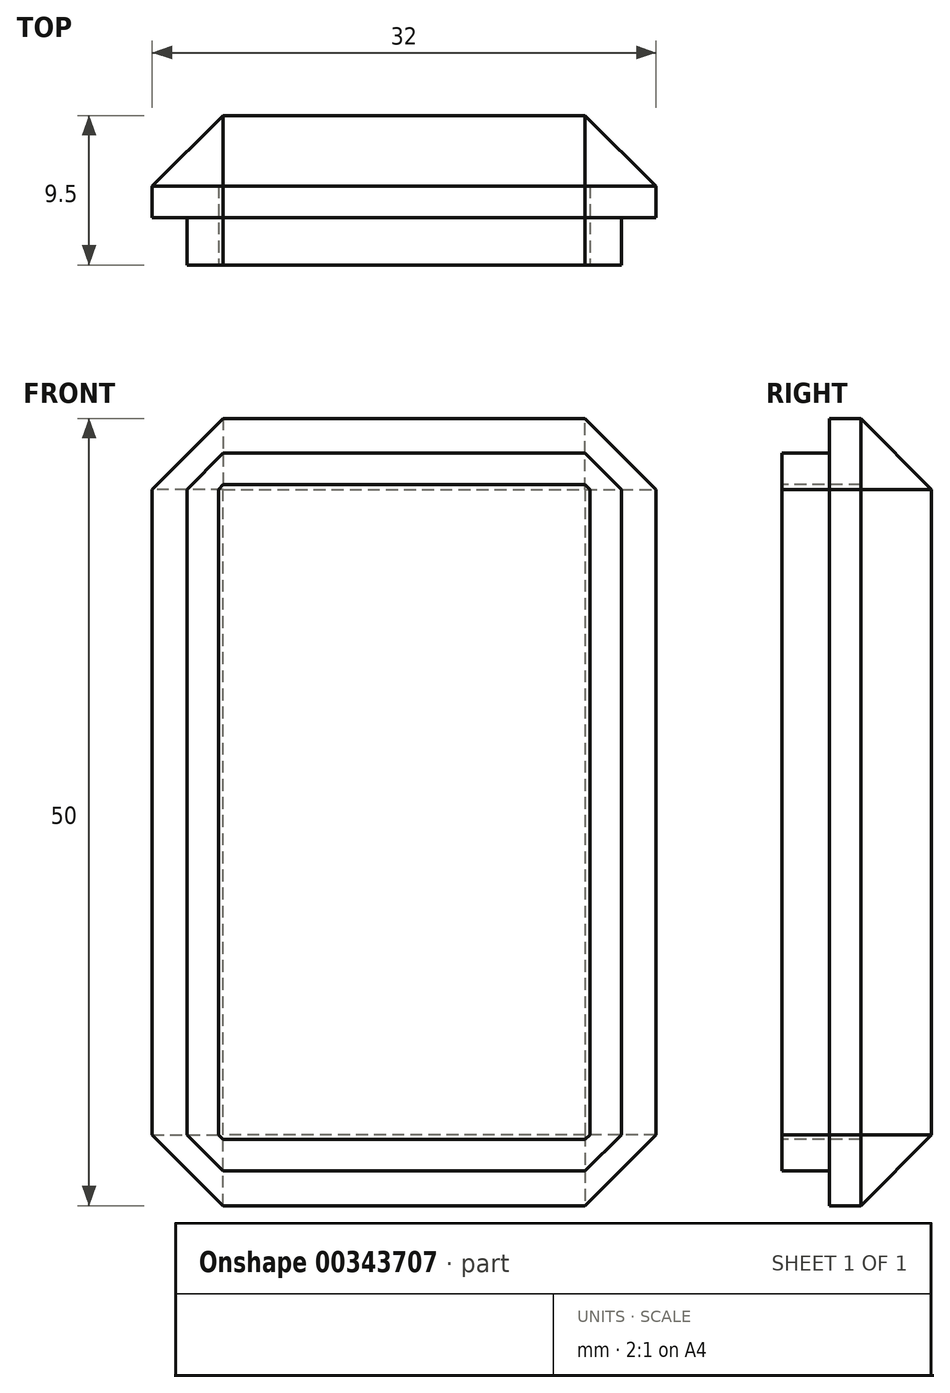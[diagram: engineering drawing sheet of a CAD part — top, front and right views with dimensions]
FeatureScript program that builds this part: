
annotation { "Feature Type Name" : "Feature", "Feature Type Description" : "" }
export const myFeature = defineFeature(function(context is Context, id is Id, definition is map)
    precondition{}
    {
        {
            var Q0;
            Q0=qCreatedBy(makeId("Front.planeOp"),FACE);
            var sketch = newSketch(context, id + "F0", { "sketchPlane" : qUnion([Q0])});
            skLineSegment(sketch, "E0.bottom", {"start": v(0, 0) * mm, "end": v(32, 0) * mm});
            skLineSegment(sketch, "E0.top", {"start": v(0, 50) * mm, "end": v(32, 50) * mm});
            skLineSegment(sketch, "E0.left", {"start": v(0, 0) * mm, "end": v(0, 50) * mm});
            skLineSegment(sketch, "E0.right", {"start": v(32, 0) * mm, "end": v(32, 50) * mm});
            skSolve(sketch);
        }
        {
            var Q0;
            Q0 = qSketchRegion(id + "F0", true);
            extrude(context, id + "F1", {"entities" : qUnion([Q0]), "depth" : 15 * mm, "offsetDistance" : 25.4 * mm});
        }
        {
            var Q0;
            Q0=makeQuery(id+"F1.opExtrude","SWEPT_FACE",FACE,{"disambiguationData":[OSD([sQuery(id+"F0.wireOp",EDGE,"E0.left")])]});
            var Q1;
            Q1=makeQuery(id+"F1.opExtrude","CAP_FACE",FACE,{"disambiguationData":[OSD([sQuery(id+"F0.wireOp",EDGE,"E0.bottom"),sQuery(id+"F0.wireOp",EDGE,"E0.top"),sQuery(id+"F0.wireOp",EDGE,"E0.left"),sQuery(id+"F0.wireOp",EDGE,"E0.right")])],"isStart":true});
            var Q2;
            Q2=makeQuery(id+"F1.opExtrude","SWEPT_FACE",FACE,{"disambiguationData":[OSD([sQuery(id+"F0.wireOp",EDGE,"E0.top")])]});
            var Q3;
            Q3=makeQuery(id+"F1.opExtrude","SWEPT_FACE",FACE,{"disambiguationData":[OSD([sQuery(id+"F0.wireOp",EDGE,"E0.right")])]});
            var Q4;
            Q4=makeQuery(id+"F1.opExtrude","SWEPT_FACE",FACE,{"disambiguationData":[OSD([sQuery(id+"F0.wireOp",EDGE,"E0.bottom")])]});
            chamfer(context, id + "F2", {"entities" : qUnion([Q0, Q1, Q2, Q3, Q4]), "width" : 4.5 * mm, "tangentPropagation" : true});
        }
        {
            var Q0;
            Q0=makeQuery(id+"F1.opExtrude","CAP_FACE",FACE,{"disambiguationData":[OSD([sQuery(id+"F0.wireOp",EDGE,"E0.bottom"),sQuery(id+"F0.wireOp",EDGE,"E0.top"),sQuery(id+"F0.wireOp",EDGE,"E0.left"),sQuery(id+"F0.wireOp",EDGE,"E0.right")])],"isStart":false});
            var sketch = newSketch(context, id + "F3", { "sketchPlane" : qUnion([Q0])});
            skLineSegment(sketch, "E1.bottom", {"start": v(-3.7, 58.79) * mm, "end": v(40.82, 58.79) * mm});
            skLineSegment(sketch, "E1.top", {"start": v(-3.7, -2.99) * mm, "end": v(40.82, -2.99) * mm});
            skLineSegment(sketch, "E1.left", {"start": v(-3.7, 58.79) * mm, "end": v(-3.7, -2.99) * mm});
            skLineSegment(sketch, "E1.right", {"start": v(40.82, 58.79) * mm, "end": v(40.82, -2.99) * mm});
            skSolve(sketch);
        }
        {
            var Q0;
            Q0 = qSketchRegion(id + "F3", true);
            extrude(context, id + "F4", {"entities" : qUnion([Q0]), "operationType" : NewBodyOperationType.REMOVE, "oppositeDirection" : true, "depth" : 8.5 * mm, "offsetDistance" : 25.4 * mm});
        }
        {
            var Q0;
            Q0=makeQuery(id+"F4.boolean.opBoolean","COPY",FACE,{"derivedFrom":makeQuery(id+"F4.opExtrude","CAP_FACE",FACE,{"disambiguationData":[OSD([sQuery(id+"F3.wireOp",EDGE,"E1.bottom"),sQuery(id+"F3.wireOp",EDGE,"E1.top"),sQuery(id+"F3.wireOp",EDGE,"E1.left"),sQuery(id+"F3.wireOp",EDGE,"E1.right")])],"isStart":false})});
            var sketch = newSketch(context, id + "F5", { "sketchPlane" : qUnion([Q0])});
            skLineSegment(sketch, "E2", {"start": v(4.5, 2.2) * mm, "end": v(27.5, 2.2) * mm});
            skLineSegment(sketch, "E3", {"start": v(27.5, 2.2) * mm, "end": v(29.8, 4.5) * mm});
            skLineSegment(sketch, "E4", {"start": v(29.8, 4.5) * mm, "end": v(29.8, 45.5) * mm});
            skLineSegment(sketch, "E5", {"start": v(29.8, 45.5) * mm, "end": v(27.5, 47.8) * mm});
            skLineSegment(sketch, "E6", {"start": v(27.5, 47.8) * mm, "end": v(4.5, 47.8) * mm});
            skLineSegment(sketch, "E7", {"start": v(4.5, 47.8) * mm, "end": v(2.2, 45.5) * mm});
            skLineSegment(sketch, "E8", {"start": v(2.2, 45.5) * mm, "end": v(2.2, 4.5) * mm});
            skLineSegment(sketch, "E9", {"start": v(2.2, 4.5) * mm, "end": v(4.5, 2.2) * mm});
            skSolve(sketch);
        }
        {
            var Q0;
            Q0 = qSketchRegion(id + "F5", true);
            extrude(context, id + "F6", {"entities" : qUnion([Q0]), "operationType" : NewBodyOperationType.ADD, "depth" : 3 * mm, "offsetDistance" : 25.4 * mm});
        }
        {
            var Q0;
            Q0=makeQuery(id+"F6.opExtrude","CAP_FACE",FACE,{"disambiguationData":[OSD([sQuery(id+"F5.wireOp",EDGE,"E2"),sQuery(id+"F5.wireOp",EDGE,"E3"),sQuery(id+"F5.wireOp",EDGE,"E4"),sQuery(id+"F5.wireOp",EDGE,"E5"),sQuery(id+"F5.wireOp",EDGE,"E6"),sQuery(id+"F5.wireOp",EDGE,"E7"),sQuery(id+"F5.wireOp",EDGE,"E8"),sQuery(id+"F5.wireOp",EDGE,"E9")])],"isStart":false});
            var sketch = newSketch(context, id + "F7", { "sketchPlane" : qUnion([Q0])});
            skLineSegment(sketch, "E10", {"start": v(4.5, 4.2) * mm, "end": v(27.5, 4.2) * mm});
            skLineSegment(sketch, "E11", {"start": v(27.5, 4.2) * mm, "end": v(27.8, 4.5) * mm});
            skLineSegment(sketch, "E12", {"start": v(27.8, 4.5) * mm, "end": v(27.8, 45.5) * mm});
            skLineSegment(sketch, "E13", {"start": v(27.8, 45.5) * mm, "end": v(27.5, 45.8) * mm});
            skLineSegment(sketch, "E14", {"start": v(27.5, 45.8) * mm, "end": v(4.5, 45.8) * mm});
            skLineSegment(sketch, "E15", {"start": v(4.5, 4.2) * mm, "end": v(4.2, 4.5) * mm});
            skLineSegment(sketch, "E16", {"start": v(4.2, 4.5) * mm, "end": v(4.2, 45.5) * mm});
            skLineSegment(sketch, "E17", {"start": v(4.2, 45.5) * mm, "end": v(4.5, 45.8) * mm});
            skSolve(sketch);
        }
        {
            var Q0;
            Q0=makeQuery(id+"F7.imprint","IMPRINT",FACE,{"disambiguationData":[TD([[makeQuery(id+"F7.imprint","IMPRINT",EDGE,{"derivedFrom":sQuery(id+"F7.wireOp",EDGE,"E10")}),1.0]])]});
            extrude(context, id + "F8", {"entities" : qUnion([Q0]), "operationType" : NewBodyOperationType.REMOVE, "oppositeDirection" : true, "depth" : 5 * mm, "offsetDistance" : 25.4 * mm});
        }
    });
